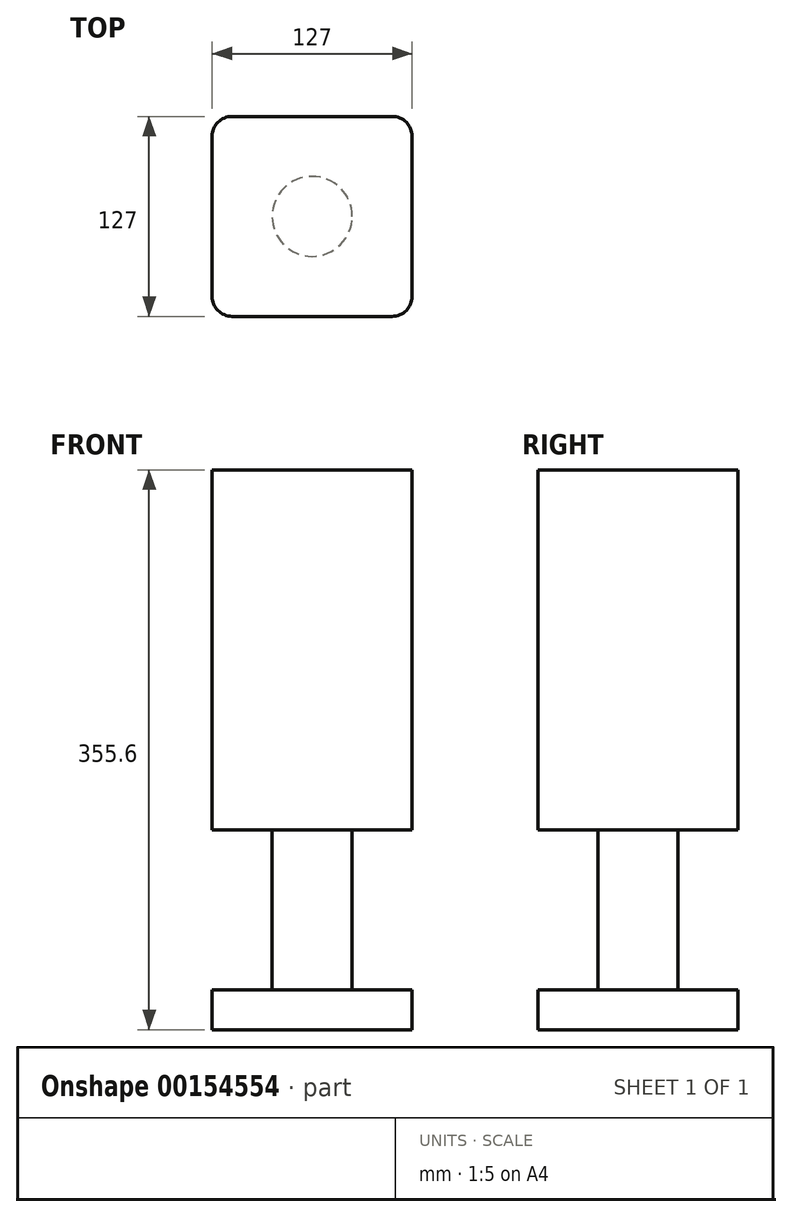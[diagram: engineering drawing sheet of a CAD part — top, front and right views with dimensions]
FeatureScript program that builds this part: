
annotation { "Feature Type Name" : "Feature", "Feature Type Description" : "" }
export const myFeature = defineFeature(function(context is Context, id is Id, definition is map)
    precondition{}
    {
        {
            var Q0;
            Q0=qCreatedBy(makeId("Top.planeOp"),FACE);
            var sketch = newSketch(context, id + "F0", { "sketchPlane" : qUnion([Q0])});
            skLineSegment(sketch, "E0.bottom", {"start": v(63.5, 63.5) * mm, "end": v(-63.5, 63.5) * mm});
            skLineSegment(sketch, "E0.top", {"start": v(63.5, -63.5) * mm, "end": v(-63.5, -63.5) * mm});
            skLineSegment(sketch, "E0.left", {"start": v(63.5, 63.5) * mm, "end": v(63.5, -63.5) * mm});
            skLineSegment(sketch, "E0.right", {"start": v(-63.5, 63.5) * mm, "end": v(-63.5, -63.5) * mm});
            skPoint(sketch, "E0.middle", {"position": v(0, 0) * mm});
            skCircle(sketch, "E1", {"center": v(0, 0) * mm, "radius": 25.4 * mm});
            skSolve(sketch);
        }
        {
            var Q0;
            Q0=makeQuery(id+"F0.imprint","IMPRINT",FACE,{"disambiguationData":[TD([[makeQuery(id+"F0.imprint","IMPRINT",EDGE,{"derivedFrom":sQuery(id+"F0.wireOp",EDGE,"E0.bottom")}),1.0]])]});
            extrude(context, id + "F1", {"entities" : qUnion([Q0]), "depth" : 25.4 * mm});
        }
        {
            var Q0;
            Q0=makeQuery(id+"F0.imprint","IMPRINT",FACE,{"disambiguationData":[TD([[makeQuery(id+"F0.imprint","IMPRINT",EDGE,{"derivedFrom":sQuery(id+"F0.wireOp",EDGE,"E1")}),1.0]])]});
            extrude(context, id + "F2", {"entities" : qUnion([Q0]), "operationType" : NewBodyOperationType.ADD, "depth" : 355.6 * mm});
        }
        {
            var Q0;
            Q0=makeQuery(id+"F2.opExtrude","CAP_FACE",FACE,{"disambiguationData":[OSD([sQuery(id+"F0.wireOp",EDGE,"E1")])],"isStart":false});
            var sketch = newSketch(context, id + "F3", { "sketchPlane" : qUnion([Q0])});
            skLineSegment(sketch, "E2.1.0", {"start": v(63.5, -63.5) * mm, "end": v(63.5, 63.5) * mm});
            skLineSegment(sketch, "E2.1.1", {"start": v(63.5, 63.5) * mm, "end": v(-63.5, 63.5) * mm});
            skLineSegment(sketch, "E2.1.2", {"start": v(-63.5, 63.5) * mm, "end": v(-63.5, -63.5) * mm});
            skLineSegment(sketch, "E2.1.3", {"start": v(-63.5, -63.5) * mm, "end": v(63.5, -63.5) * mm});
            skSolve(sketch);
        }
        {
            var Q0;
            Q0=makeQuery(id+"F3.imprint","IMPRINT",FACE,{"disambiguationData":[TD([[makeQuery(id+"F3.imprint","IMPRINT",EDGE,{"derivedFrom":sQuery(id+"F3.wireOp",EDGE,"E2.1.0")}),1.0]])]});
            var Q1;
            Q1=makeQuery(id+"F3.imprint","IMPRINT",FACE,{"disambiguationData":[TD([[makeQuery(id+"F3.imprint","IMPRINT",EDGE,{"derivedFrom":makeQuery(id+"F2.opExtrude","CAP_EDGE",EDGE,{"disambiguationData":[OSD([sQuery(id+"F0.wireOp",EDGE,"E1")])],"isStart":false})}),1.0]])]});
            extrude(context, id + "F4", {"entities" : qUnion([Q0, Q1]), "operationType" : NewBodyOperationType.ADD, "oppositeDirection" : true, "depth" : 228.6 * mm});
        }
        {
            var Q0;
            Q0=makeQuery(id+"F4.opExtrude","SWEPT_EDGE",EDGE,{"disambiguationData":[OSD([sQuery(id+"F3.wireOp",EDGE,"E2.1.0"),sQuery(id+"F3.wireOp",EDGE,"E2.1.3")])]});
            var Q1;
            Q1=makeQuery(id+"F4.opExtrude","SWEPT_EDGE",EDGE,{"disambiguationData":[OSD([sQuery(id+"F3.wireOp",EDGE,"E2.1.0"),sQuery(id+"F3.wireOp",EDGE,"E2.1.1")])]});
            var Q2;
            Q2=makeQuery(id+"F4.opExtrude","SWEPT_EDGE",EDGE,{"disambiguationData":[OSD([sQuery(id+"F3.wireOp",EDGE,"E2.1.2"),sQuery(id+"F3.wireOp",EDGE,"E2.1.3")])]});
            var Q3;
            Q3=makeQuery(id+"F1.opExtrude","SWEPT_EDGE",EDGE,{"disambiguationData":[OSD([sQuery(id+"F0.wireOp",EDGE,"E0.top"),sQuery(id+"F0.wireOp",EDGE,"E0.left")])]});
            var Q4;
            Q4=makeQuery(id+"F1.opExtrude","SWEPT_EDGE",EDGE,{"disambiguationData":[OSD([sQuery(id+"F0.wireOp",EDGE,"E0.bottom"),sQuery(id+"F0.wireOp",EDGE,"E0.left")])]});
            var Q5;
            Q5=makeQuery(id+"F1.opExtrude","SWEPT_EDGE",EDGE,{"disambiguationData":[OSD([sQuery(id+"F0.wireOp",EDGE,"E0.top"),sQuery(id+"F0.wireOp",EDGE,"E0.right")])]});
            var Q6;
            Q6=makeQuery(id+"F4.opExtrude","SWEPT_EDGE",EDGE,{"disambiguationData":[OSD([sQuery(id+"F3.wireOp",EDGE,"E2.1.1"),sQuery(id+"F3.wireOp",EDGE,"E2.1.2")])]});
            var Q7;
            Q7=makeQuery(id+"F1.opExtrude","SWEPT_EDGE",EDGE,{"disambiguationData":[OSD([sQuery(id+"F0.wireOp",EDGE,"E0.bottom"),sQuery(id+"F0.wireOp",EDGE,"E0.right")])]});
            fillet(context, id + "F5", {"entities" : qUnion([Q0, Q1, Q2, Q3, Q4, Q5, Q6, Q7]), "radius" : 12.7 * mm, "tangentPropagation" : true, "allowEdgeOverflow" : false});
        }
    });
